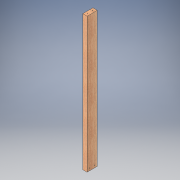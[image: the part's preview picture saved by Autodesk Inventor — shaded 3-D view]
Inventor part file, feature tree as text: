
AUTODESK INVENTOR PART (.ipt)
format: ipt  version: 2017 (Build 210142000, 142)  size: 126,464 bytes
history: native  units: in
note: dims shown in document units (in); Inventor stores cm internally (conversion verified against a paired STEP export)
features: extrude x3, sketch x3
ambient origin geometry x8: Origin, YZ Plane, XZ Plane, XY Plane, X Axis, Y Axis, Z Axis, Center Point
bodies: Solid1 (feature_tree)
feature tree (6):
  extrude  "Wood"  Depth=3.5in
  extrude  "Extrusion4"  Depth=46.5in
  extrude  "Extrusion5"  Depth=1.5in
  sketch  "Sketch1"  dims[d0=1.5in d1=3.5in]
  sketch  "Sketch4"  dims[d2=46.5in d3=0.0in d11=0.1875in]
  sketch  "Sketch5"  dims[d12=1.5in d13=0.0in d14=1.5in d15=0.1875in d16=1.5in d17=0.0in]
